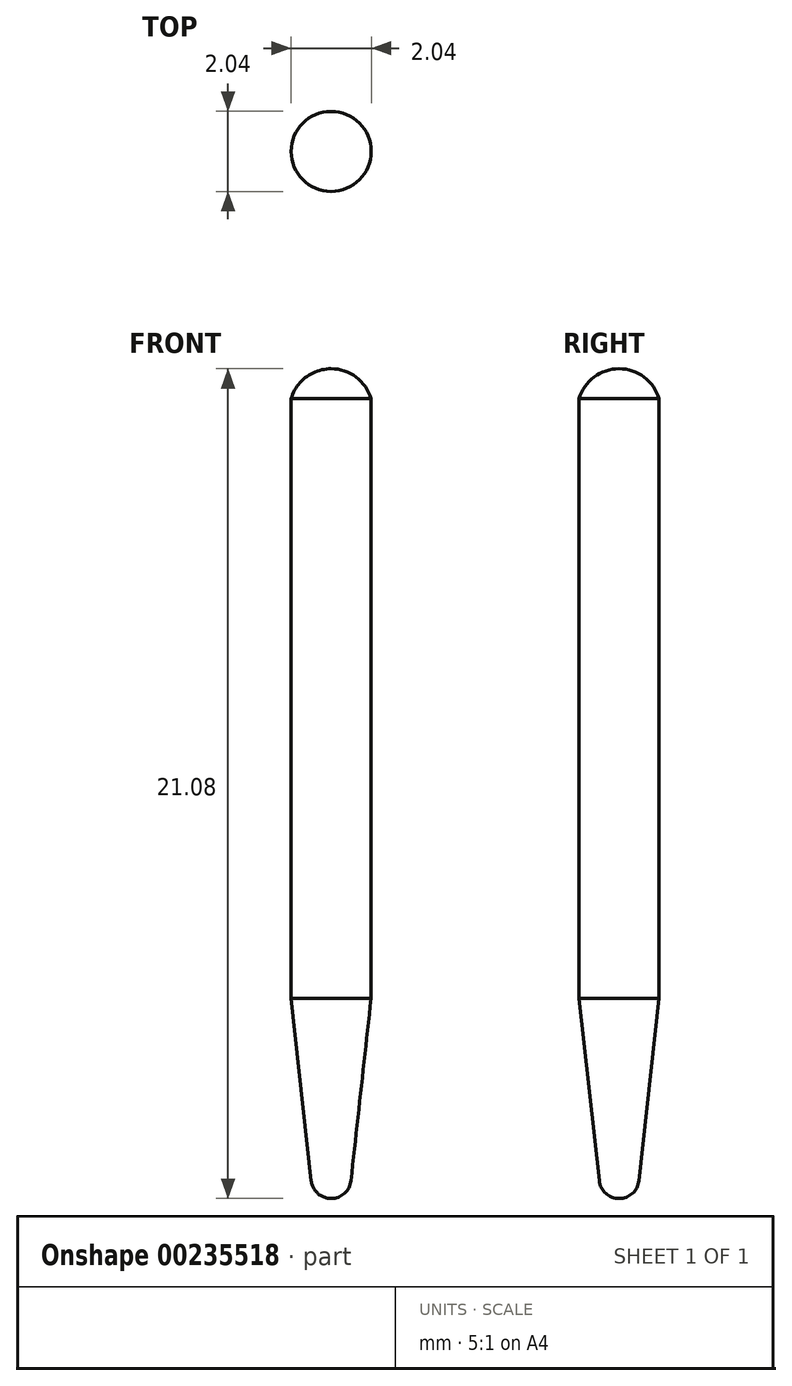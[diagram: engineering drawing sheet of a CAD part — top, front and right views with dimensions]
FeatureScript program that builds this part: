
annotation { "Feature Type Name" : "Feature", "Feature Type Description" : "" }
export const myFeature = defineFeature(function(context is Context, id is Id, definition is map)
    precondition{}
    {
        {
            var Q0;
            Q0=qCreatedBy(makeId("Front.planeOp"),FACE);
            var sketch = newSketch(context, id + "F0", { "sketchPlane" : qUnion([Q0])});
            skLineSegment(sketch, "E0", {"start": v(1.02, 3.97) * mm, "end": v(1.02, -11.27) * mm});
            skLineSegment(sketch, "E1", {"start": v(1.02, 3.97) * mm, "end": v(-1.02, 3.97) * mm});
            skLineSegment(sketch, "E2", {"start": v(-1.02, 3.97) * mm, "end": v(-1.02, -11.27) * mm});
            skLineSegment(sketch, "E3", {"start": v(-1.02, -11.27) * mm, "end": v(1.02, -11.27) * mm});
            skArc(sketch, "E4", {"start": v(-0.5, -15.9) * mm, "mid": v(0, -16.35) * mm, "end": v(0.5, -15.9) * mm});
            skPoint(sketch, "E4.centerSnap0", {"position": v(0, -11.27) * mm});
            skLineSegment(sketch, "E5", {"start": v(-1.02, -11.27) * mm, "end": v(-0.5, -15.9) * mm});
            skLineSegment(sketch, "E6", {"start": v(1.02, -11.27) * mm, "end": v(0.5, -15.9) * mm});
            skArc(sketch, "E7", {"start": v(1.02, 3.97) * mm, "mid": v(0, 4.73) * mm, "end": v(-1.02, 3.97) * mm});
            skLineSegment(sketch, "E8", {"start": v(0, 3.67) * mm, "end": v(0, -17.43) * mm});
            skLineSegment(sketch, "E9", {"start": v(0, 3.67) * mm, "end": v(0, 6.23) * mm});
            skSolve(sketch);
        }
        {
            var Q0;
            {var subQ5=sQuery(id+"F0.wireOp",EDGE,"E2");Q0=makeQuery(id+"F0.imprint","IMPRINT",FACE,{"disambiguationData":[TD([[makeQuery(id+"F0.imprint","IMPRINT",EDGE,{"derivedFrom":subQ5}),1.0]])]});}
            var Q1;
            {var subQ0=sQuery(id+"F0.wireOp",EDGE,"E7");var subQ3=sQuery(id+"F0.wireOp",EDGE,"E9");var subQ5=makeQuery(id+"F0.imprint","INTERSECT",VERTEX,{"derivedFrom":[subQ0,subQ3]});Q1=makeQuery(id+"F0.imprint","IMPRINT",FACE,{"disambiguationData":[TD([[makeQuery(id+"F0.imprint","IMPRINT",EDGE,{"disambiguationData":[TD([[subQ5,1.0]])],"derivedFrom":subQ3}),1.0]])]});}
            var Q2;
            {var subQ0=sQuery(id+"F0.wireOp",EDGE,"E5");Q2=makeQuery(id+"F0.imprint","IMPRINT",FACE,{"disambiguationData":[TD([[makeQuery(id+"F0.imprint","IMPRINT",EDGE,{"derivedFrom":subQ0}),1.0]])]});}
            var Q3;
            Q3=sQuery(id+"F0.wireOp",EDGE,"E8");
            revolve(context, id + "F1", {"entities" : qUnion([Q0, Q1, Q2]), "axis" : qUnion([Q3]), "revolveType" : RevolveType.FULL});
        }
    });
